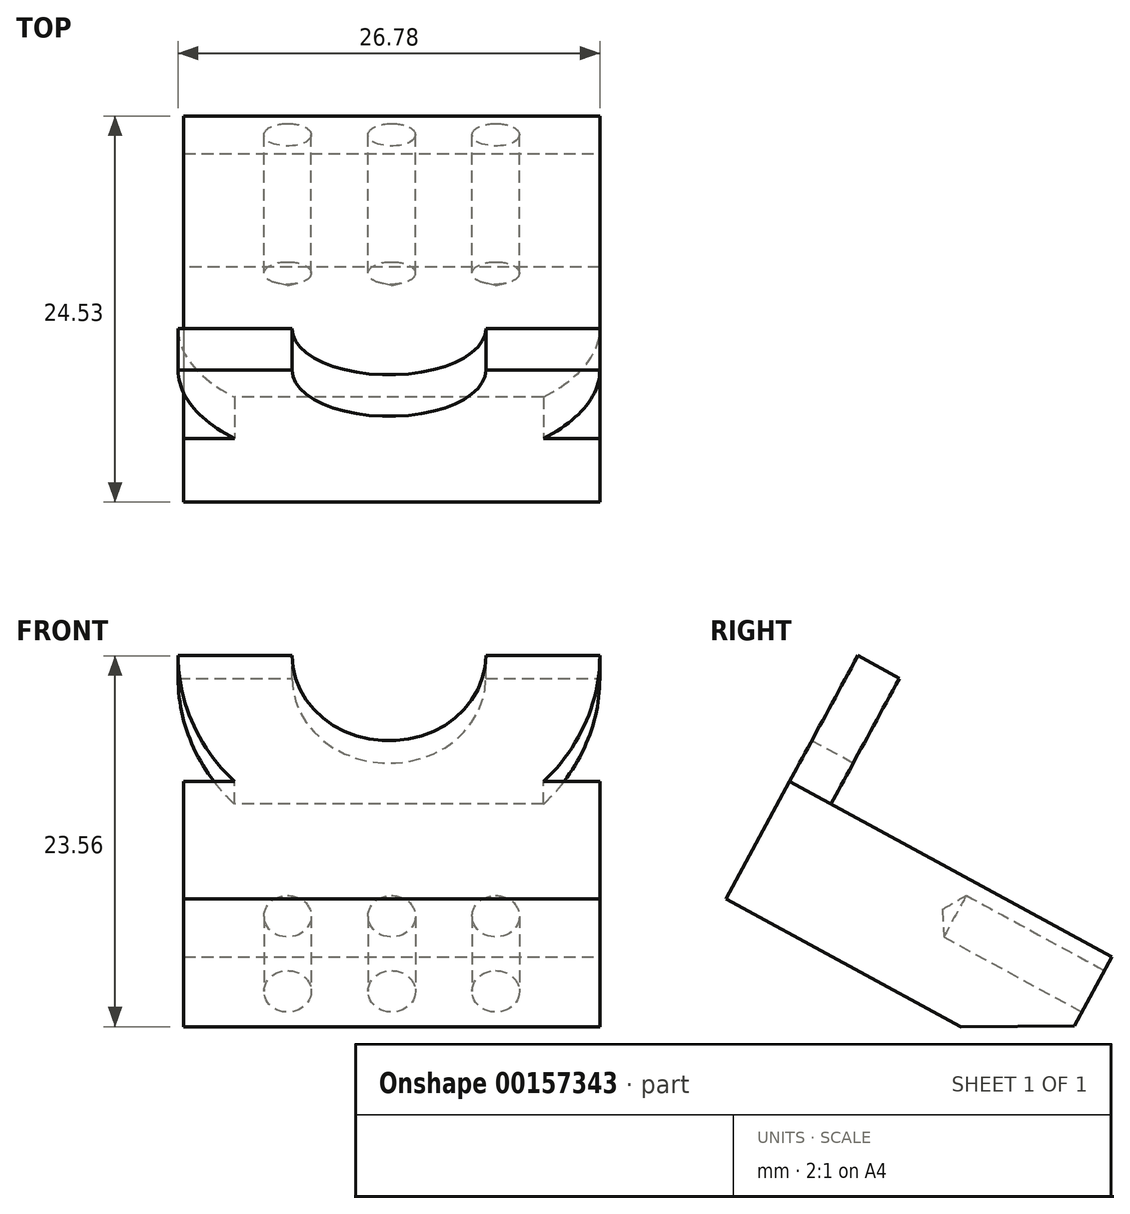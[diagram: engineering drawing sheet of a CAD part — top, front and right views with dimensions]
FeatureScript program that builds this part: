
annotation { "Feature Type Name" : "Feature", "Feature Type Description" : "" }
export const myFeature = defineFeature(function(context is Context, id is Id, definition is map)
    precondition{}
    {
        {
            var Q0;
            Q0=qCreatedBy(makeId("Right.planeOp"),FACE);
            var sketch = newSketch(context, id + "F0", { "sketchPlane" : qUnion([Q0])});
            skLineSegment(sketch, "E0.0.2", {"start": v(-21.9, 21) * mm, "end": v(-30.58, 5) * mm});
            skLineSegment(sketch, "E0.0.3", {"start": v(-30.58, 5) * mm, "end": v(-23.77, 1.3) * mm});
            skLineSegment(sketch, "E1", {"start": v(-30.58, 5) * mm, "end": v(-34.63, -2.45) * mm});
            skLineSegment(sketch, "E2", {"start": v(-23.77, 1.3) * mm, "end": v(-25.78, -2.4) * mm});
            skLineSegment(sketch, "E3", {"start": v(-30.58, 5) * mm, "end": v(-45.52, 13.11) * mm});
            skLineSegment(sketch, "E4", {"start": v(-45.52, 13.11) * mm, "end": v(-49.57, 5.66) * mm});
            skLineSegment(sketch, "E5", {"start": v(-34.63, -2.45) * mm, "end": v(-49.57, 5.66) * mm});
            skLineSegment(sketch, "E6", {"start": v(-34.63, -2.45) * mm, "end": v(-25.78, -2.4) * mm});
            skPoint(sketch, "E0.0.0.start.orphan", {"position": v(-16.96, -2.4) * mm});
            skSolve(sketch);
        }
        {
            var Q0;
            Q0=makeQuery(id+"F0.imprint","IMPRINT",FACE,{"disambiguationData":[TD([[makeQuery(id+"F0.imprint","IMPRINT",EDGE,{"derivedFrom":sQuery(id+"F0.wireOp",EDGE,"E1")}),-1.0]])]});
            var Q1;
            Q1=makeQuery(id+"F0.imprint","IMPRINT",FACE,{"disambiguationData":[TD([[makeQuery(id+"F0.imprint","IMPRINT",EDGE,{"derivedFrom":sQuery(id+"F0.wireOp",EDGE,"E0.0.3")}),-1.0]])]});
            extrude(context, id + "F1", {"entities" : qUnion([Q0, Q1]), "depth" : 26.44 * mm});
        }
        {
            var Q0;
            Q0=makeQuery(id+"F1.opExtrude","SWEPT_FACE",FACE,{"disambiguationData":[OSD([sQuery(id+"F0.wireOp",EDGE,"E4")])]});
            var sketch = newSketch(context, id + "F2", { "sketchPlane" : qUnion([Q0])});
            skLineSegment(sketch, "E7.0.0", {"start": v(0, -10.2) * mm, "end": v(0, -18.68) * mm});
            skLineSegment(sketch, "E7.0.1", {"start": v(0, -18.68) * mm, "end": v(26.44, -18.68) * mm});
            skLineSegment(sketch, "E7.0.2", {"start": v(26.44, -18.68) * mm, "end": v(26.44, -10.2) * mm});
            skLineSegment(sketch, "E7.0.3", {"start": v(26.44, -10.2) * mm, "end": v(0, -10.2) * mm});
            skPoint(sketch, "E8", {"position": v(13.22, -10.2) * mm});
            skPoint(sketch, "E9", {"position": v(13.05, -1.1) * mm});
            skArc(sketch, "E10", {"start": v(6.9, -1.1) * mm, "mid": v(13.05, -7.24) * mm, "end": v(19.2, -1.1) * mm});
            skArc(sketch, "E11", {"start": v(-0.34, -1.1) * mm, "mid": v(13.05, -14.48) * mm, "end": v(26.44, -1.1) * mm});
            skLineSegment(sketch, "E12", {"start": v(-0.34, -1.1) * mm, "end": v(6.9, -1.1) * mm});
            skLineSegment(sketch, "E13.trimOffspring", {"start": v(19.2, -1.1) * mm, "end": v(26.44, -1.1) * mm});
            skSolve(sketch);
        }
        {
            var Q0;
            {var subQ0=sQuery(id+"F2.wireOp",EDGE,"E11");var subQ1=sQuery(id+"F2.wireOp",EDGE,"E7.0.3");var subQ2=makeQuery(id+"F2.imprint","INTERSECT",VERTEX,{"disambiguationData":[OD(0.0)],"derivedFrom":[subQ1,subQ0]});Q0=makeQuery(id+"F2.imprint","IMPRINT",FACE,{"disambiguationData":[TD([[makeQuery(id+"F2.imprint","IMPRINT",EDGE,{"disambiguationData":[TD([[subQ2,-1.0]])],"derivedFrom":subQ1}),1.0]])]});}
            var Q1;
            Q1=makeQuery(id+"F2.imprint","IMPRINT",FACE,{"disambiguationData":[TD([[makeQuery(id+"F2.imprint","IMPRINT",EDGE,{"derivedFrom":sQuery(id+"F2.wireOp",EDGE,"E10")}),-1.0]])]});
            extrude(context, id + "F3", {"entities" : qUnion([Q0, Q1]), "operationType" : NewBodyOperationType.ADD, "oppositeDirection" : true, "depth" : 3 * mm});
        }
        {
            var Q0;
            Q0=makeQuery(id+"F1.opExtrude","CAP_FACE",FACE,{"disambiguationData":[OSD([sQuery(id+"F0.wireOp",EDGE,"E0.0.3"),sQuery(id+"F0.wireOp",EDGE,"E2"),sQuery(id+"F0.wireOp",EDGE,"E3"),sQuery(id+"F0.wireOp",EDGE,"E4"),sQuery(id+"F0.wireOp",EDGE,"E5"),sQuery(id+"F0.wireOp",EDGE,"E6")])],"isStart":false});
            var sketch = newSketch(context, id + "F4", { "sketchPlane" : qUnion([Q0])});
            skLineSegment(sketch, "E14.0.0", {"start": v(-49.57, 5.66) * mm, "end": v(-34.63, -2.45) * mm});
            skLineSegment(sketch, "E14.0.1", {"start": v(-34.63, -2.45) * mm, "end": v(-25.78, -2.4) * mm});
            skLineSegment(sketch, "E14.0.2", {"start": v(-25.78, -2.4) * mm, "end": v(-23.77, 1.3) * mm});
            skLineSegment(sketch, "E14.0.3", {"start": v(-23.77, 1.3) * mm, "end": v(-45.52, 13.11) * mm});
            skLineSegment(sketch, "E14.0.4", {"start": v(-45.52, 13.11) * mm, "end": v(-49.57, 5.66) * mm});
            skLineSegment(sketch, "E15", {"start": v(-25.04, 2) * mm, "end": v(-27.42, -2.4) * mm});
            skSolve(sketch);
        }
        {
            var Q0;
            {var subQ0=sQuery(id+"F4.wireOp",EDGE,"E14.0.2");Q0=makeQuery(id+"F4.imprint","IMPRINT",FACE,{"disambiguationData":[TD([[makeQuery(id+"F4.imprint","IMPRINT",EDGE,{"derivedFrom":subQ0}),-1.0]])]});}
            extrude(context, id + "F5", {"entities" : qUnion([Q0]), "operationType" : NewBodyOperationType.REMOVE, "endBound" : BoundingType.THROUGH_ALL, "oppositeDirection" : true, "depth" : 25 * mm});
        }
        {
            var Q0;
            Q0=makeQuery(id+"F5.boolean.opBoolean","COPY",FACE,{"derivedFrom":makeQuery(id+"F5.opExtrude","SWEPT_FACE",FACE,{"disambiguationData":[OSD([sQuery(id+"F4.wireOp",EDGE,"E15")])]})});
            var sketch = newSketch(context, id + "F6", { "sketchPlane" : qUnion([Q0])});
            skLineSegment(sketch, "E16.0.0", {"start": v(0, -10.2) * mm, "end": v(-26.44, -10.2) * mm});
            skLineSegment(sketch, "E16.0.1", {"start": v(-26.44, -10.2) * mm, "end": v(-26.44, -15.2) * mm});
            skLineSegment(sketch, "E16.0.2", {"start": v(-26.44, -15.2) * mm, "end": v(0, -15.2) * mm});
            skLineSegment(sketch, "E16.0.3", {"start": v(0, -15.2) * mm, "end": v(0, -10.2) * mm});
            skPoint(sketch, "E17", {"position": v(-13.22, -12.7) * mm});
            skPoint(sketch, "E17.positionSnap0", {"position": v(-26.44, -12.7) * mm});
            skPoint(sketch, "E17.positionSnap1", {"position": v(-13.22, -10.2) * mm});
            skPoint(sketch, "E18", {"position": v(-19.83, -12.7) * mm});
            skPoint(sketch, "E19", {"position": v(-6.6, -12.7) * mm});
            skSolve(sketch);
        }
        {
            var Q0;
            Q0=sQuery(id+"F6.wireOp",VERTEX,"E18");
            var Q1;
            Q1=sQuery(id+"F6.wireOp",VERTEX,"E17");
            var Q2;
            Q2=sQuery(id+"F6.wireOp",VERTEX,"E19");
            var Q3;
            Q3=makeQuery(id+"F1.opExtrude","SWEPT_BODY",BODY,{"disambiguationData":[OSD([sQuery(id+"F0.wireOp",EDGE,"E0.0.3"),sQuery(id+"F0.wireOp",EDGE,"E2"),sQuery(id+"F0.wireOp",EDGE,"E3"),sQuery(id+"F0.wireOp",EDGE,"E4"),sQuery(id+"F0.wireOp",EDGE,"E5"),sQuery(id+"F0.wireOp",EDGE,"E6")])]});
            hole(context, id + "F7", {"style" : HoleStyle.SIMPLE, "endStyle" : HoleEndStyle.BLIND, "holeDiameter" : 3 * mm, "holeDepth" : 10 * mm, "locations" : qUnion([Q0, Q1, Q2]), "scope" : qUnion([Q3])});
        }
    });
